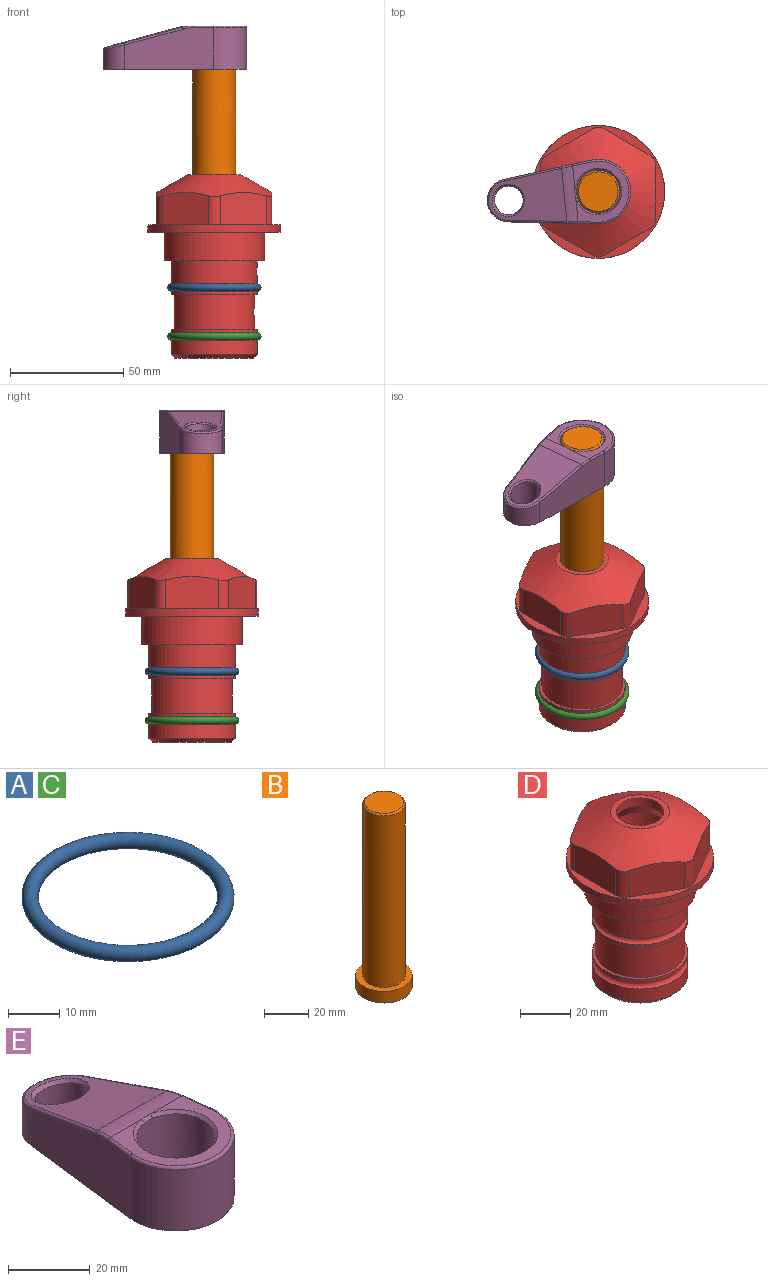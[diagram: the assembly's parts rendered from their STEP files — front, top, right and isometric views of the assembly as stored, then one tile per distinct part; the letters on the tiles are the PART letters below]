
ASSEMBLY  parts=5 mates=5
PART A: 1 faces, bbox 44.7x44.7x3.2 mm
  f0: torus R=19.05mm, axis (0,0,1), area 1193.9mm2
PART B: 6 faces, bbox 25.4x25.4x101.6 mm
  f0: plane 17.46x17.46mm, normal (0,0,1), area 239.5mm2, adj f5
  f1: plane 25.4x25.4mm, normal (0,0,-1), area 506.7mm2, adj f2
  f2: cylinder r=12.7mm len=25.4mm, axis (0,0,1), area 506.7mm2, adj f1,f3
  f3: plane 25.4x25.4mm, normal (0,0,1), area 221.7mm2, adj f2,f4
  f4: cylinder r=9.53mm len=94.46mm, axis (0,0,1), area 5653mm2, adj f3,f5
  f5: cone r=8.73mm half-angle=45deg, axis (0,0,-1), area 64.4mm2, adj f0,f4
PART C: same geometry as A
PART D: 36 faces, bbox 58.7x58.7x81 mm
  f0: cylinder r=17.78mm len=35.56mm, axis (0,0,1), area 1670.8mm2, adj f23,f24,f31
  f1: cylinder r=19.05mm len=38.1mm, axis (0,0,1), area 1191.9mm2, adj f26,f27,f30
  f2: plane 58.66x58.66mm, normal (0,0,-1), area 1150.6mm2, adj f3,f28
  f3: cylinder r=29.33mm len=58.66mm, axis (0,0,-1), area 585.1mm2, adj f2,f4
  f4: plane 58.66x58.66mm, normal (0,0,1), area 475.9mm2, adj f3,f5,f6,f7,f8,f9,f10,f11
  f5: plane 20.32x14.34mm, normal (-0.5,0.87,0), area 324.4mm2, adj f4,f15,f16,f17
  f6: plane 20.32x14.34mm, normal (0.5,0.87,0), area 324.4mm2, adj f4,f14,f15,f17
  f7: plane 23.48x14.34mm, normal (1,0,0), area 324.4mm2, adj f4,f13,f14,f17
  f8: plane 20.32x14.34mm, normal (0.5,-0.87,0), area 324.4mm2, adj f4,f12,f13,f17
  f9: plane 20.32x14.34mm, normal (-0.5,-0.87,0), area 324.4mm2, adj f4,f11,f12,f17
  f10: plane 23.48x14.34mm, normal (-1,0,0), area 324.4mm2, adj f4,f11,f16,f17
  f11: cylinder r=5.08mm len=12.85mm, axis (0,0,-1), area 67.2mm2, adj f4,f9,f10,f17
  f12: cylinder r=5.08mm len=12.85mm, axis (0,0,-1), area 67.2mm2, adj f4,f8,f9,f17
  f13: cylinder r=5.08mm len=12.85mm, axis (0,0,-1), area 67.2mm2, adj f4,f7,f8,f17
  f14: cylinder r=5.08mm len=12.85mm, axis (0,0,-1), area 67.2mm2, adj f4,f6,f7,f17
  f15: cylinder r=5.08mm len=12.85mm, axis (0,0,-1), area 67.2mm2, adj f4,f5,f6,f17
  f16: cylinder r=5.08mm len=12.85mm, axis (0,0,-1), area 67.2mm2, adj f4,f5,f10,f17
  f17: cone r=11.73mm half-angle=60deg, axis (0,0,-1), area 2071.8mm2, adj f5,f6,f7,f8,f9,f10,f11,f12
  f18: plane 23.46x23.46mm, normal (0,0,1), area 147.4mm2, adj f17,f35
  f19: plane 34.93x34.93mm, normal (0,0,-1), area 958mm2, adj f29
  f20: cylinder r=19.05mm len=38.1mm, axis (0,0,1), area 760.1mm2, adj f21,f29
  f21: torus R=19.05mm, axis (0,0,1), area 565.3mm2, adj f20,f22
  f22: cylinder r=19.05mm len=38.1mm, axis (0,0,1), area 190mm2, adj f21,f23
  f23: plane 38.1x38.1mm, normal (0,0,1), area 146.9mm2, adj f0,f22
  f24: plane 38.1x38.1mm, normal (0,0,-1), area 146.9mm2, adj f0,f25
  f25: cylinder r=19.05mm len=38.1mm, axis (0,0,1), area 190mm2, adj f24,f26
  f26: torus R=19.05mm, axis (0,0,1), area 565.3mm2, adj f1,f25
  f27: plane 44.45x44.45mm, normal (0,0,-1), area 411.7mm2, adj f1,f28
  f28: cylinder r=22.23mm len=44.45mm, axis (0,0,1), area 1773.5mm2, adj f2,f27
  f29: cone r=19.05mm half-angle=45deg, axis (0,0,1), area 257.5mm2, adj f19,f20
  f30: cylinder r=3.17mm len=6.75mm, axis (-1,0,0), area 128mm2, adj f1,f33
  f31: cylinder r=3.17mm len=6.35mm, axis (-1,0,0), area 102.5mm2, adj f0,f33
  f32: plane 25.4x25.4mm, normal (0,0,1), area 506.7mm2, adj f33
  f33: cylinder r=12.7mm len=66.42mm, axis (0,0,-1), area 5236.2mm2, adj f30,f31,f32,f34
  f34: cone r=9.53mm half-angle=30deg, axis (0,0,-1), area 443.4mm2, adj f33,f35
  f35: cylinder r=9.53mm len=19.05mm, axis (0,0,-1), area 240.9mm2, adj f18,f34
PART E: 31 faces, bbox 31.7x65.5x19.8 mm
  f0: plane 39.12x18.26mm, normal (0.99,0.12,0), area 612.2mm2, adj f1,f4,f7,f11,f13,f15
  f1: cylinder r=9.53mm len=18.91mm, axis (0,0,-1), area 296.1mm2, adj f0,f2,f7,f17
  f2: plane 39.12x18.26mm, normal (-0.99,0.12,0), area 612.2mm2, adj f1,f4,f7,f12,f14,f16
  f3: cylinder r=6.35mm len=12.7mm, axis (0,0,-1), area 362.4mm2, adj f7,f18
  f4: cylinder r=14.29mm len=28.58mm, axis (0,0,-1), area 882.2mm2, adj f0,f2,f7,f10
  f5: cylinder r=9.53mm len=19.05mm, axis (0,0,-1), area 1092.6mm2, adj f7,f19,f20
  f6: plane 26.99x23.69mm, normal (0,0,1), area 216.2mm2, adj f9,f10,f11,f12,f19
  f7: plane 63.5x28.58mm, normal (0,0,-1), area 661.8mm2, adj f0,f1,f2,f3,f4,f5,f22,f23
  f8: plane 33.52x23.6mm, normal (0,0.26,0.97), area 486mm2, adj f9,f15,f16,f17,f18
  f9: cylinder r=19.05mm len=24.72mm, axis (1,0,0), area 120.4mm2, adj f6,f8,f13,f14,f20
  f10: torus R=13.49mm, axis (0,0,1), area 59mm2, adj f4,f6,f11,f12
  f11: cylinder r=0.79mm len=8.67mm, axis (0.12,-0.99,0), area 10.8mm2, adj f0,f6,f10,f13
  f12: cylinder r=0.79mm len=8.67mm, axis (0.12,0.99,0), area 10.8mm2, adj f2,f6,f10,f14
  f13: bspline ~4.95x1.42mm, area 6.1mm2, adj f0,f9,f11,f15
  f14: bspline ~4.95x1.42mm, area 6.1mm2, adj f2,f9,f12,f16
  f15: cylinder r=0.79mm len=25.95mm, axis (0.12,-0.96,0.26), area 32.9mm2, adj f0,f8,f13,f17
  f16: cylinder r=0.79mm len=25.95mm, axis (0.12,0.96,-0.26), area 32.9mm2, adj f2,f8,f14,f17
  f17: bspline ~18.91x8.38mm, area 30mm2, adj f1,f8,f15,f16
  f18: bspline ~14.29x14.29mm, area 48.3mm2, adj f3,f8
  f19: cone r=9.53mm half-angle=45deg, axis (0,0,1), area 66.5mm2, adj f5,f6,f20
  f20: bspline ~3.22x0.96mm, area 3.5mm2, adj f5,f9,f19
  f21: plane 2.75x2.72mm, normal (0,0,-1), area 2.9mm2, adj f23,f25,f28
  f22: plane 23.05x15.88mm, normal (-0.99,-0.12,0), area 323.6mm2, adj f7,f25,f26,f27,f28,f29
  f23: plane 23.05x15.88mm, normal (0.99,-0.12,0), area 323.6mm2, adj f7,f21,f25,f27,f28,f30
  f24: cylinder r=9.53mm len=10.69mm, axis (0,0,-1), area 114.7mm2, adj f7,f27,f29,f30
  f25: cylinder r=12.7mm len=20.59mm, axis (0,0,-1), area 381.1mm2, adj f7,f21,f22,f23,f26,f28
  f26: plane 2.75x2.72mm, normal (0,0,-1), area 2.9mm2, adj f22,f25,f28
  f27: plane 19.72x18.37mm, normal (0,-0.26,-0.97), area 291.8mm2, adj f22,f23,f24,f28,f29,f30
  f28: cylinder r=15.88mm len=19.92mm, axis (1,0,0), area 54.8mm2, adj f21,f22,f23,f25,f26,f27
  f29: cylinder r=1.59mm len=11mm, axis (0,0,-1), area 34.7mm2, adj f7,f22,f24,f27
  f30: cylinder r=1.59mm len=11mm, axis (0,0,-1), area 34.7mm2, adj f7,f23,f24,f27
PLACE A at identity
PLACE B rot(axis=(0,0,1),95.5deg) t=(0,0,27.55)mm
PLACE C t=(0,0,-21.59)mm
PLACE D at identity fixed
PLACE E rot(axis=(0,0,1),95.5deg) t=(0,0,27.55)mm
MATE fastened A.f0 <-> D.f0  axis (0,0,1) through (0,0,-24.51)mm
MATE fastened B.f2 <-> E.f4  axis (0,0,-1) through (0,0,90.26)mm
MATE fastened A.f0 <-> D.f0  axis (0,0,1) through (0,0,-24.51)mm
MATE fastened C.f0 <-> D.f0  axis (0,0,1) through (0,0,-46.1)mm
MATE cylindrical B.f2 <-> D.f0  axis (0,0,-1) through (0,0,-10.55)mm
